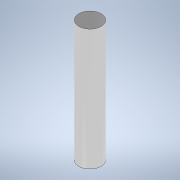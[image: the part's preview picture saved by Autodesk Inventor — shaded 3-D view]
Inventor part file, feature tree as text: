
AUTODESK INVENTOR PART (.ipt)
format: ipt  version: 2022 (Build 260153000, 153)  size: 95,744 bytes
history: native  units: mm
features: extrude x1, sketch x1
ambient origin geometry x8: Origin, YZ Plane, XZ Plane, XY Plane, X Axis, Y Axis, Z Axis, Center Point
bodies: Solid1 (feature_tree)
feature tree (2):
  extrude  "Extrusion1"  Depth=12.0mm TaperAngle=0.0deg
  sketch  "Sketch1"  dims[d0=2.2mm d1=12.0mm d2=0.0mm]
